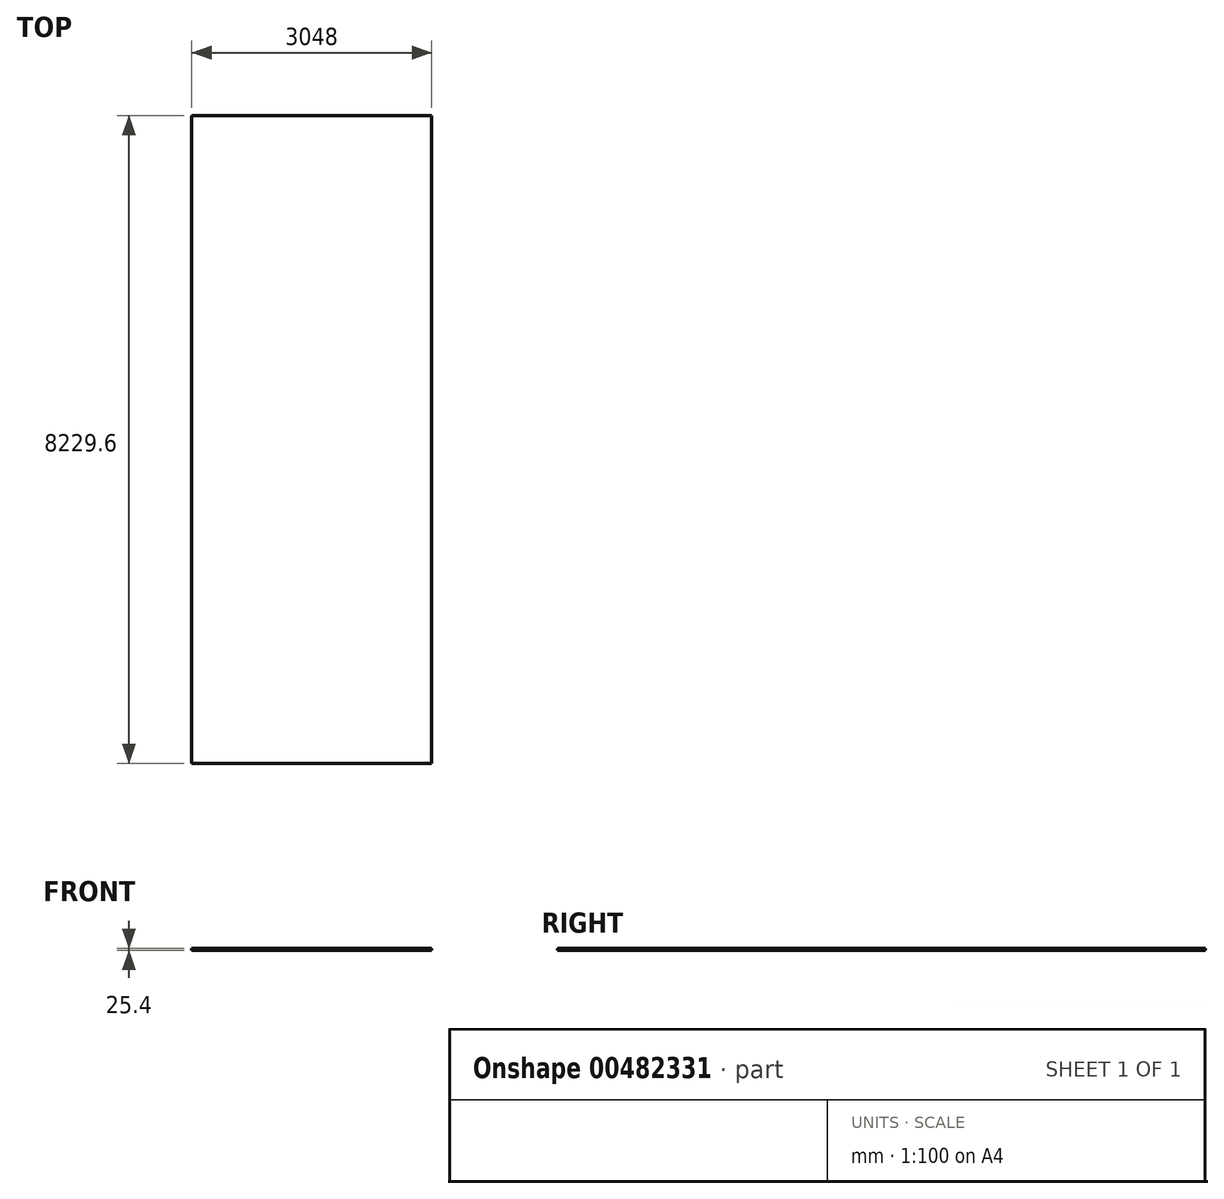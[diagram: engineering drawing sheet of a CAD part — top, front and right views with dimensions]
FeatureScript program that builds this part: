
annotation { "Feature Type Name" : "Feature", "Feature Type Description" : "" }
export const myFeature = defineFeature(function(context is Context, id is Id, definition is map)
    precondition{}
    {
        {
            var Q0;
            Q0=qCreatedBy(makeId("Top.planeOp"),FACE);
            var sketch = newSketch(context, id + "F0", { "sketchPlane" : qUnion([Q0])});
            skLineSegment(sketch, "E0.bottom", {"start": v(-3048, 8229.6) * mm, "end": v(0, 8229.6) * mm});
            skLineSegment(sketch, "E0.top", {"start": v(-3048, 0) * mm, "end": v(0, 0) * mm});
            skLineSegment(sketch, "E0.left", {"start": v(-3048, 8229.6) * mm, "end": v(-3048, 0) * mm});
            skLineSegment(sketch, "E0.right", {"start": v(0, 8229.6) * mm, "end": v(0, 0) * mm});
            skSolve(sketch);
        }
        {
            var Q0;
            Q0 = qSketchRegion(id + "F0", true);
            extrude(context, id + "F1", {"entities" : qUnion([Q0]), "depth" : 25.4 * mm, "offsetDistance" : 25.4 * mm});
        }
    });
